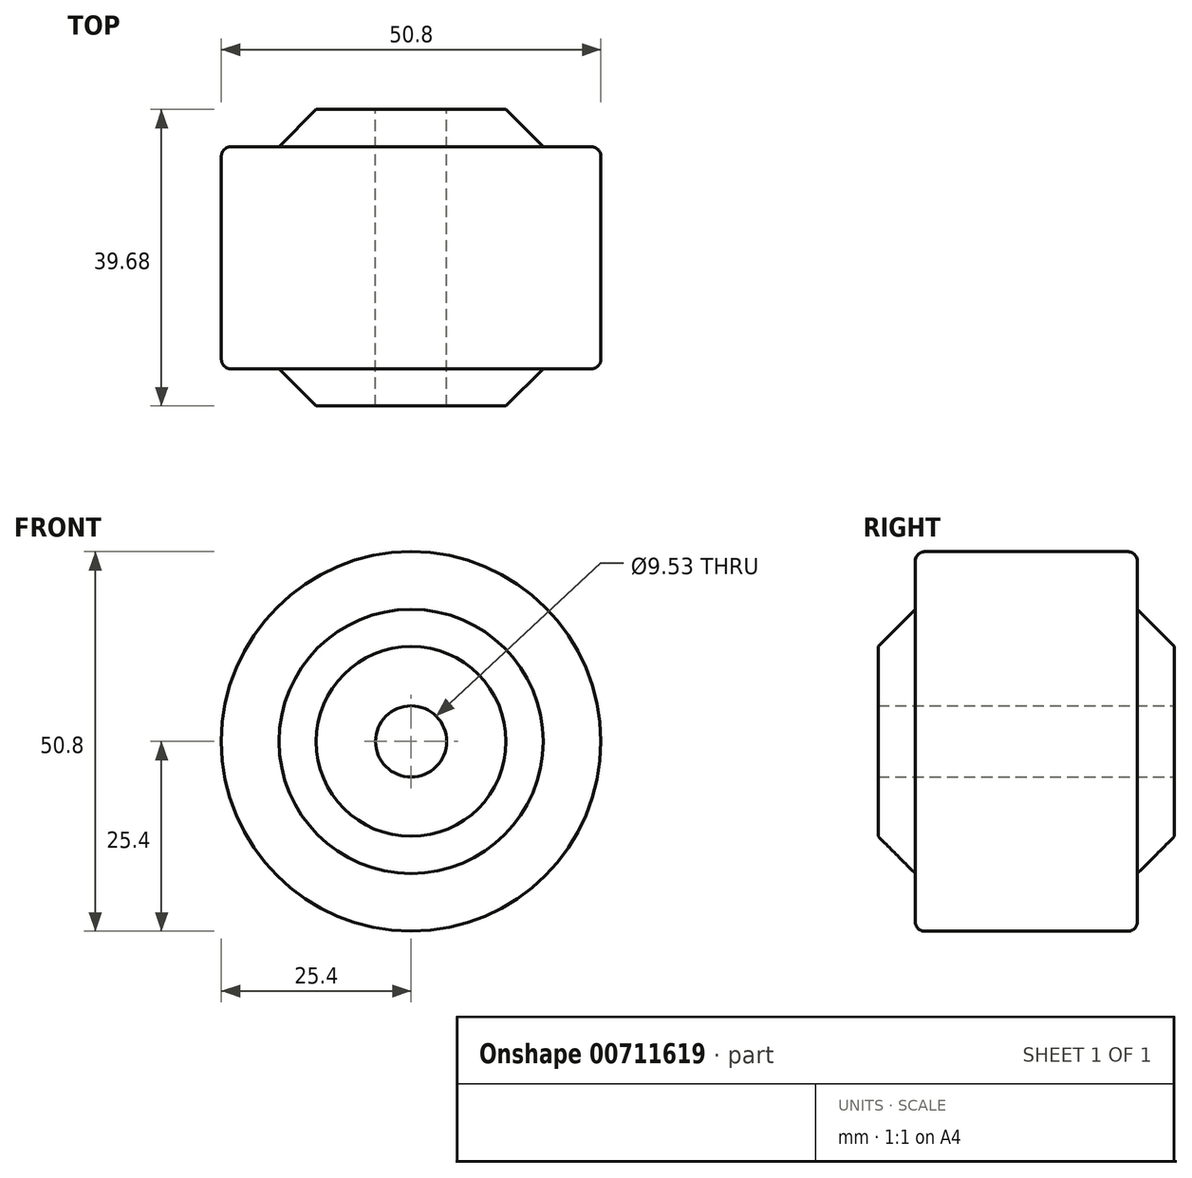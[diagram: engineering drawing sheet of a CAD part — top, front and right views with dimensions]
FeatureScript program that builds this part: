
annotation { "Feature Type Name" : "Feature", "Feature Type Description" : "" }
export const myFeature = defineFeature(function(context is Context, id is Id, definition is map)
    precondition{}
    {
        {
            var Q0;
            Q0=qCreatedBy(makeId("Front.planeOp"),FACE);
            var sketch = newSketch(context, id + "F0", { "sketchPlane" : qUnion([Q0])});
            skCircle(sketch, "E0", {"center": v(0, 0) * mm, "radius": 25.4 * mm});
            skCircle(sketch, "E1", {"center": v(0, 0) * mm, "radius": 4.76 * mm});
            skCircle(sketch, "E2", {"center": v(0, 0) * mm, "radius": 19.05 * mm});
            skSolve(sketch);
        }
        {
            var Q0;
            Q0=makeQuery(id+"F0.imprint","IMPRINT",FACE,{"disambiguationData":[TD([[makeQuery(id+"F0.imprint","IMPRINT",EDGE,{"derivedFrom":sQuery(id+"F0.wireOp",EDGE,"E1")}),-1.0]])]});
            extrude(context, id + "F1", {"entities" : qUnion([Q0]), "endBound" : BoundingType.SYMMETRIC, "depth" : 39.67 * mm, "offsetDistance" : 25.4 * mm});
        }
        {
            var Q0;
            Q0 = qSketchRegion(id + "F0", true);
            extrude(context, id + "F2", {"entities" : qUnion([Q0]), "operationType" : NewBodyOperationType.ADD, "endBound" : BoundingType.SYMMETRIC, "depth" : 29.72 * mm, "offsetDistance" : 25.4 * mm});
        }
        {
            var Q0;
            Q0=makeQuery(id+"F1.opExtrude","CAP_EDGE",EDGE,{"disambiguationData":[OSD([sQuery(id+"F0.wireOp",EDGE,"E2")])],"isStart":false});
            var Q1;
            Q1=makeQuery(id+"F1.opExtrude","CAP_EDGE",EDGE,{"disambiguationData":[OSD([sQuery(id+"F0.wireOp",EDGE,"E2")])],"isStart":true});
            chamfer(context, id + "F3", {"entities" : qUnion([Q0, Q1]), "width" : 6.35 * mm, "tangentPropagation" : true});
        }
        {
            var Q0;
            Q0=makeQuery(id+"F2.opExtrude","CAP_EDGE",EDGE,{"disambiguationData":[OSD([sQuery(id+"F0.wireOp",EDGE,"E0")])],"isStart":false});
            var Q1;
            Q1=makeQuery(id+"F2.opExtrude","CAP_EDGE",EDGE,{"disambiguationData":[OSD([sQuery(id+"F0.wireOp",EDGE,"E0")])],"isStart":true});
            fillet(context, id + "F4", {"entities" : qUnion([Q0, Q1]), "radius" : 1.27 * mm, "tangentPropagation" : true, "allowEdgeOverflow" : false});
        }
    });
